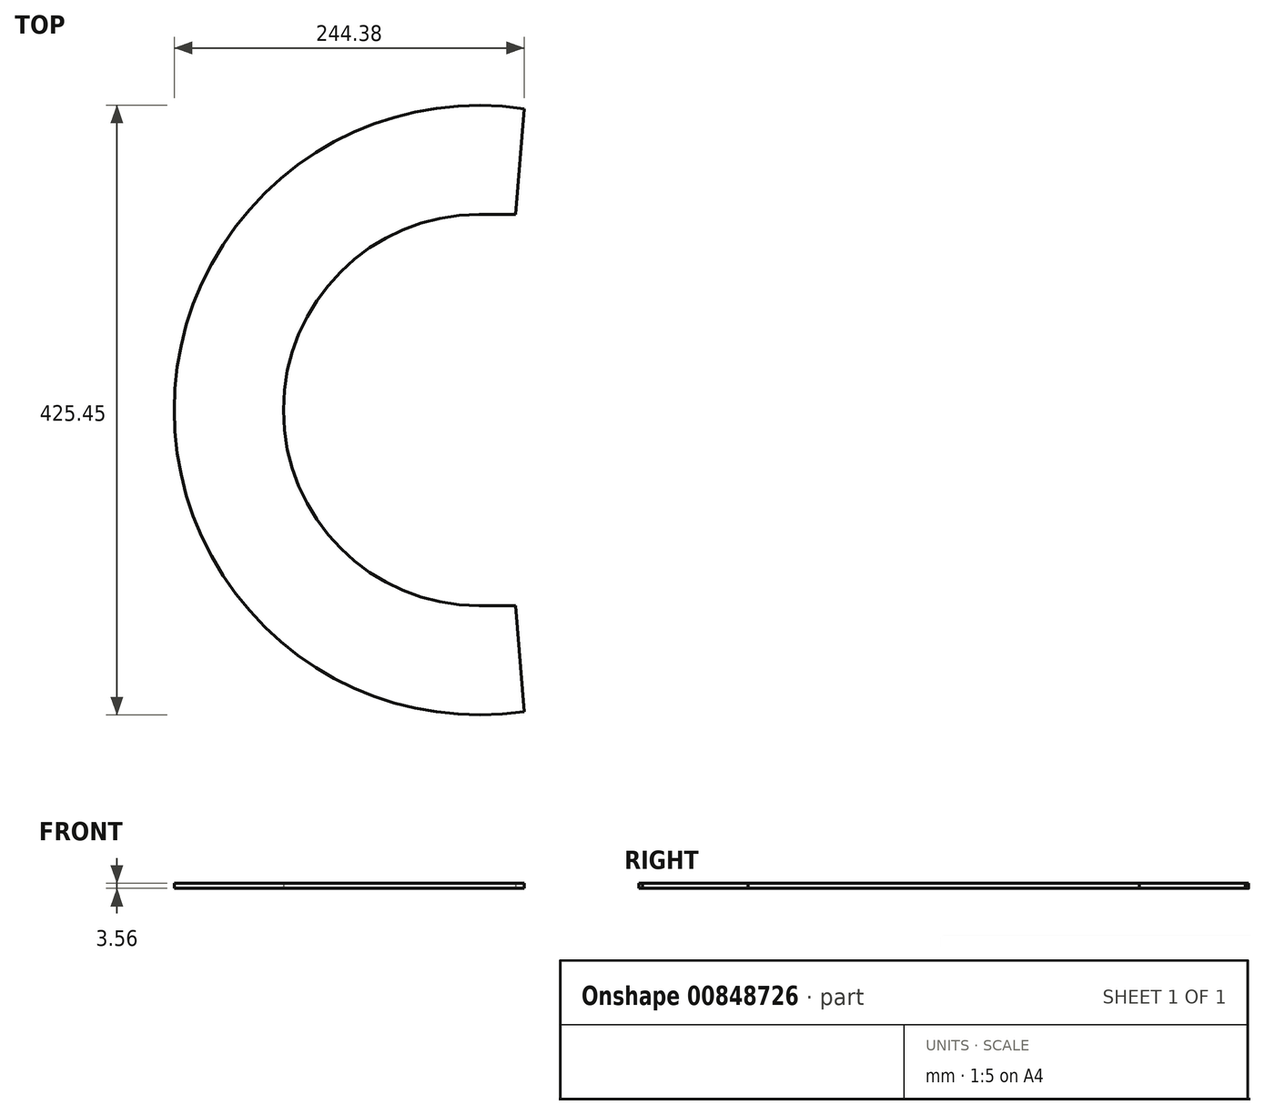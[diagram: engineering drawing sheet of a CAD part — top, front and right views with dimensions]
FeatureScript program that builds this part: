
annotation { "Feature Type Name" : "Feature", "Feature Type Description" : "" }
export const myFeature = defineFeature(function(context is Context, id is Id, definition is map)
    precondition{}
    {
        {
            var Q0;
            Q0=qCreatedBy(makeId("Top.planeOp"),FACE);
            var sketch = newSketch(context, id + "F0", { "sketchPlane" : qUnion([Q0])});
            skArc(sketch, "E0", {"start": v(0, 136.53) * mm, "mid": v(-136.53, 0) * mm, "end": v(0, -136.53) * mm});
            skArc(sketch, "E1", {"start": v(31.66, 210.36) * mm, "mid": v(-212.73, 0) * mm, "end": v(31.66, -210.36) * mm});
            skLineSegment(sketch, "E2", {"start": v(0, -136.53) * mm, "end": v(0, 136.53) * mm});
            skLineSegment(sketch, "E3", {"start": v(25.6, 136.53) * mm, "end": v(31.66, 210.36) * mm});
            skLineSegment(sketch, "E4", {"start": v(0, 0) * mm, "end": v(109.4, 0) * mm, "construction": true});
            skLineSegment(sketch, "E5.MirrorCS", {"start": v(25.6, -136.53) * mm, "end": v(31.66, -210.36) * mm});
            skPoint(sketch, "E6.orphan", {"position": v(0, -212.73) * mm});
            skPoint(sketch, "E7.orphan", {"position": v(0, 212.73) * mm});
            skLineSegment(sketch, "E8", {"start": v(0, 136.53) * mm, "end": v(25.6, 136.53) * mm});
            skLineSegment(sketch, "E9.MirrorCS", {"start": v(0, -136.53) * mm, "end": v(25.6, -136.53) * mm});
            skPoint(sketch, "E10.orphan", {"position": v(25.4, -134.14) * mm});
            skPoint(sketch, "E11.orphan", {"position": v(25.4, 134.14) * mm});
            skSolve(sketch);
        }
        {
            var Q0;
            Q0=makeQuery(id+"F0.imprint","IMPRINT",FACE,{"disambiguationData":[TD([[makeQuery(id+"F0.imprint","IMPRINT",EDGE,{"derivedFrom":sQuery(id+"F0.wireOp",EDGE,"E0")}),-1.0]])]});
            extrude(context, id + "F1", {"entities" : qUnion([Q0]), "depth" : 3.56 * mm, "offsetDistance" : 25.4 * mm});
        }
    });
